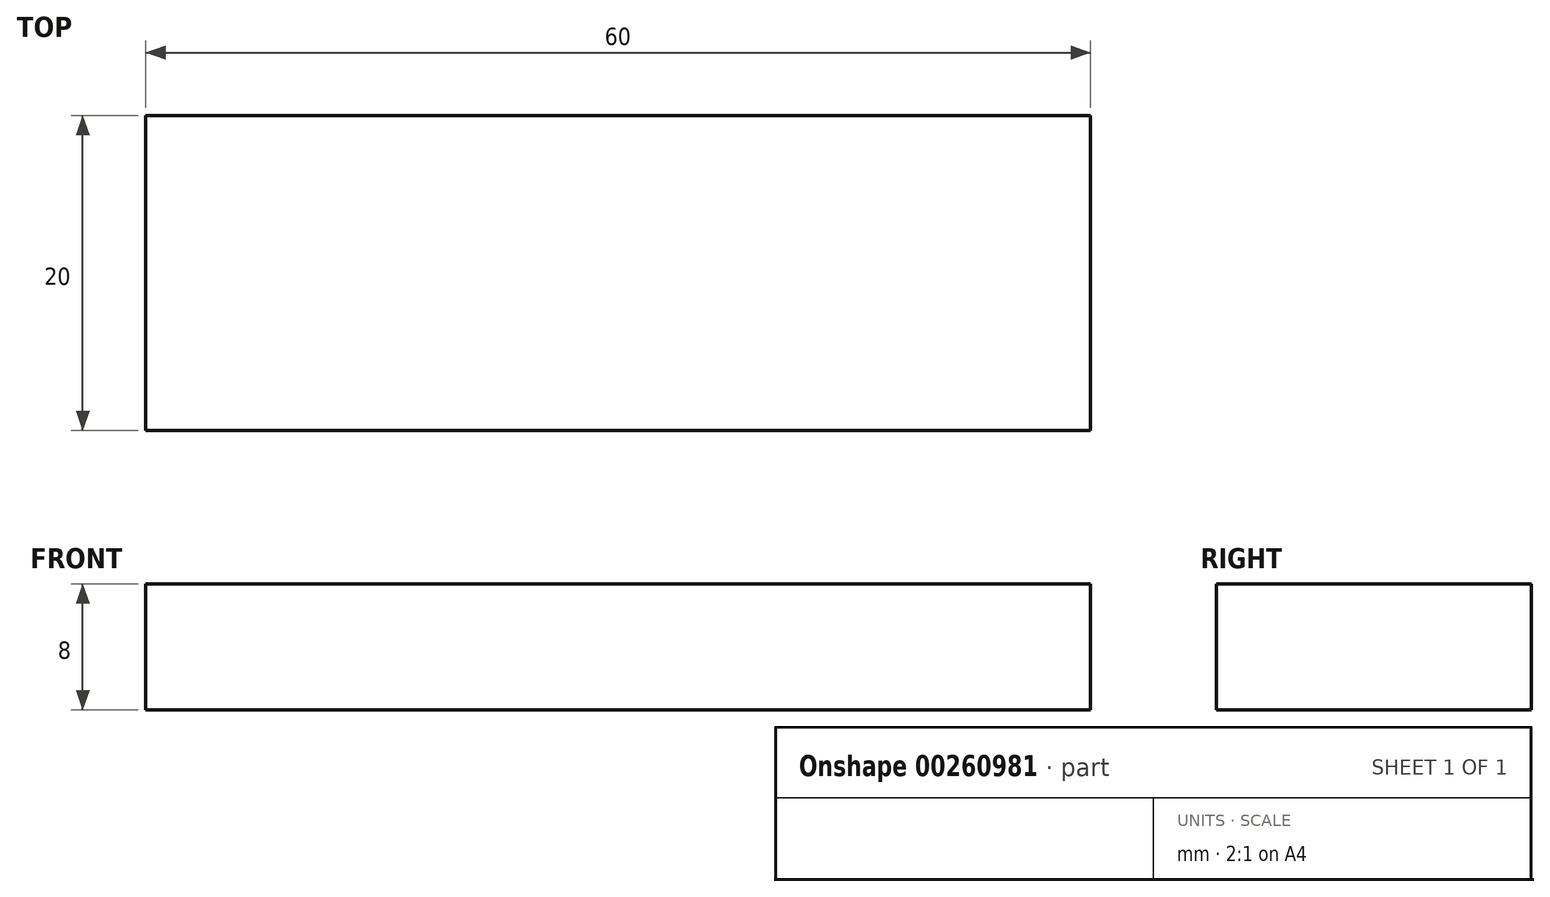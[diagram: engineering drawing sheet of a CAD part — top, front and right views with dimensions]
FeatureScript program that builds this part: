
annotation { "Feature Type Name" : "Feature", "Feature Type Description" : "" }
export const myFeature = defineFeature(function(context is Context, id is Id, definition is map)
    precondition{}
    {
        {
            var Q0;
            Q0=qCreatedBy(makeId("Top.planeOp"),FACE);
            var sketch = newSketch(context, id + "F0", { "sketchPlane" : qUnion([Q0])});
            skLineSegment(sketch, "E0", {"start": v(0, 0) * mm, "end": v(60, 0) * mm});
            skLineSegment(sketch, "E1", {"start": v(60, 0) * mm, "end": v(60, 20) * mm});
            skLineSegment(sketch, "E2", {"start": v(60, 20) * mm, "end": v(0, 20) * mm});
            skLineSegment(sketch, "E3", {"start": v(0, 20) * mm, "end": v(0, 0) * mm});
            skSolve(sketch);
        }
        {
            var Q0;
            Q0=makeQuery(id+"F0.imprint","IMPRINT",FACE,{"disambiguationData":[TD([[makeQuery(id+"F0.imprint","IMPRINT",EDGE,{"derivedFrom":sQuery(id+"F0.wireOp",EDGE,"E0")}),1.0]])]});
            extrude(context, id + "F1", {"entities" : qUnion([Q0]), "depth" : 8 * mm});
        }
    });
